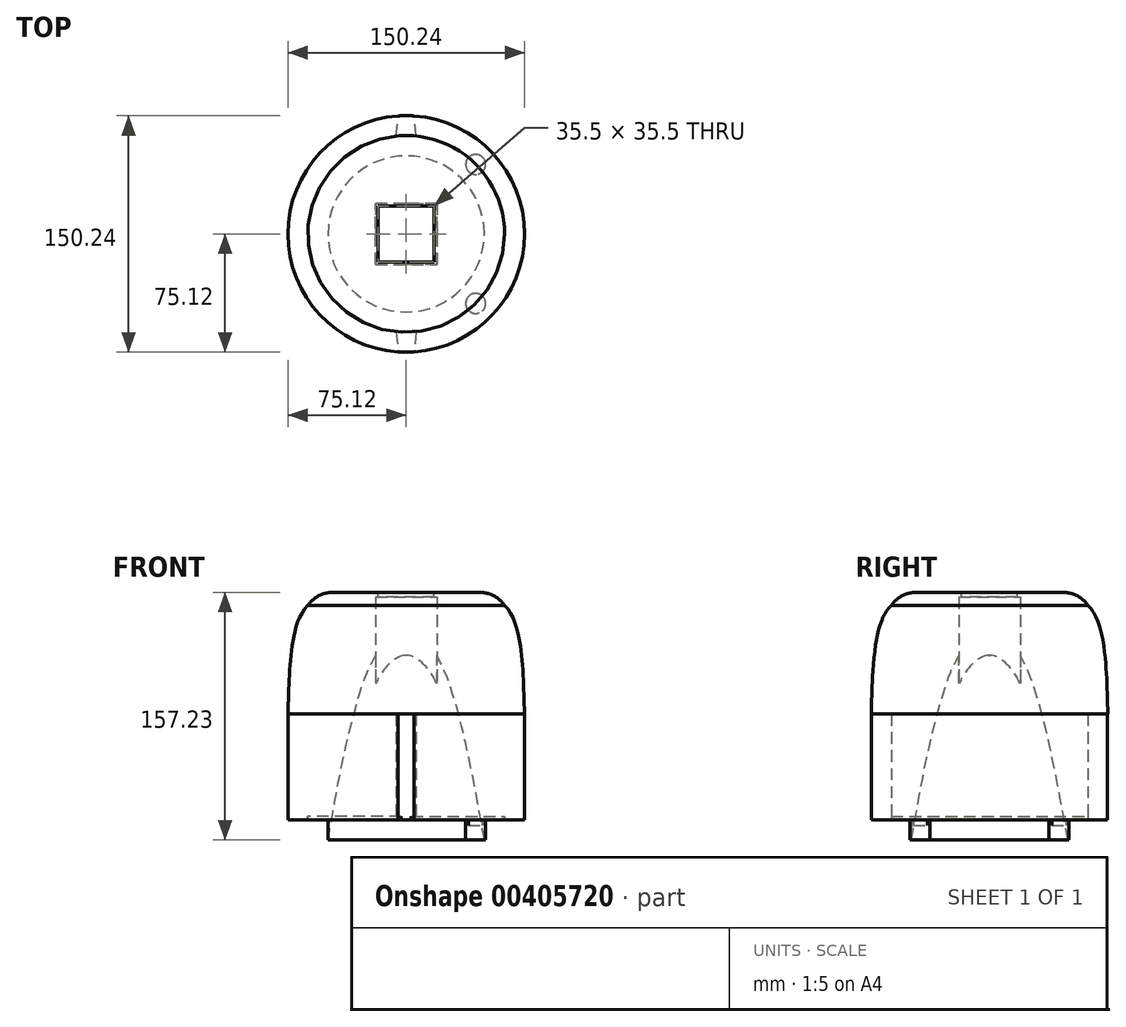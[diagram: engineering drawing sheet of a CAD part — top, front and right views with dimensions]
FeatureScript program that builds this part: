
annotation { "Feature Type Name" : "Feature", "Feature Type Description" : "" }
export const myFeature = defineFeature(function(context is Context, id is Id, definition is map)
    precondition{}
    {
        {
            var Q0;
            Q0=qCreatedBy(makeId("Front.planeOp"),FACE);
            var sketch = newSketch(context, id + "F0", { "sketchPlane" : qUnion([Q0])});
            skLineSegment(sketch, "E0", {"start": v(0, 0) * mm, "end": v(0, 152.4) * mm});
            skLineSegment(sketch, "E1", {"start": v(-50.8, 152.4) * mm, "end": v(-45.72, 152.4) * mm});
            skLineSegment(sketch, "E2", {"start": v(-45.72, 152.4) * mm, "end": v(-45.72, 157.4) * mm});
            skLineSegment(sketch, "E3", {"start": v(-75.12, 0) * mm, "end": v(-62.42, 0) * mm});
            skArc(sketch, "E4", {"start": v(-50.8, 152.4) * mm, "mid": v(-60.05, 76.46) * mm, "end": v(-62.42, 0) * mm});
            skLineSegment(sketch, "E5", {"start": v(-75.12, 0) * mm, "end": v(-75.12, 80) * mm});
            skFitSpline(sketch, "E6", {"points": [v(-75.12, 80) * mm, v(-65.64, 145) * mm, v(-45.72, 157.4) * mm], "startDerivative": vector(3.22, 125.97) * mm, "endDerivative": vector(60.37, 19.92) * mm});
            skSolve(sketch);
        }
        {
            var Q0;
            Q0=makeQuery(id+"F0.imprint","IMPRINT",FACE,{"disambiguationData":[TD([[makeQuery(id+"F0.imprint","IMPRINT",EDGE,{"derivedFrom":sQuery(id+"F0.wireOp",EDGE,"E1")}),1.0]])]});
            var Q1;
            Q1=sQuery(id+"F0.wireOp",EDGE,"E0");
            revolve(context, id + "F1", {"entities" : qUnion([Q0]), "axis" : qUnion([Q1]), "revolveType" : RevolveType.FULL});
        }
        {
            var Q0;
            Q0=qCreatedBy(makeId("Top.planeOp"),FACE);
            var sketch = newSketch(context, id + "F2", { "sketchPlane" : qUnion([Q0])});
            skLineSegment(sketch, "E7.bottom", {"start": v(19.42, 19.42) * mm, "end": v(-19.42, 19.42) * mm});
            skLineSegment(sketch, "E7.top", {"start": v(19.42, -19.42) * mm, "end": v(-19.42, -19.42) * mm});
            skLineSegment(sketch, "E7.left", {"start": v(19.42, 19.42) * mm, "end": v(19.42, -19.42) * mm});
            skLineSegment(sketch, "E7.right", {"start": v(-19.42, 19.42) * mm, "end": v(-19.42, -19.42) * mm});
            skCircle(sketch, "E8", {"center": v(0, 0) * mm, "radius": 62.5 * mm});
            skSolve(sketch);
        }
        {
            var Q0;
            Q0=makeQuery(id+"F2.imprint","IMPRINT",FACE,{"disambiguationData":[TD([[makeQuery(id+"F2.imprint","IMPRINT",EDGE,{"derivedFrom":sQuery(id+"F2.wireOp",EDGE,"E7.bottom")}),-1.0]])]});
            extrude(context, id + "F3", {"entities" : qUnion([Q0]), "operationType" : NewBodyOperationType.ADD, "depth" : 157.39 * mm});
        }
        {
            var Q0;
            Q0=qCreatedBy(makeId("Front.planeOp"),FACE);
            var sketch = newSketch(context, id + "F4", { "sketchPlane" : qUnion([Q0])});
            skLineSegment(sketch, "E9", {"start": v(-68.96, 155.44) * mm, "end": v(-59.58, 163.5) * mm});
            skLineSegment(sketch, "E10", {"start": v(-46.58, 157.23) * mm, "end": v(0, 157.23) * mm});
            skLineSegment(sketch, "E11", {"start": v(0, 157.23) * mm, "end": v(0, 165.56) * mm});
            skLineSegment(sketch, "E12", {"start": v(0, 165.56) * mm, "end": v(-59.58, 163.5) * mm});
            skLineSegment(sketch, "E13", {"start": v(-62.5, 148.83) * mm, "end": v(-68.96, 155.44) * mm});
            skArc(sketch, "E14", {"start": v(-46.58, 157.23) * mm, "mid": v(-55.58, 155) * mm, "end": v(-62.5, 148.83) * mm});
            skSolve(sketch);
        }
        {
            var Q0;
            Q0=qCreatedBy(makeId("Front.planeOp"),FACE);
            var sketch = newSketch(context, id + "F5", { "sketchPlane" : qUnion([Q0])});
            skLineSegment(sketch, "E15", {"start": v(0, 0) * mm, "end": v(-19.43, 0) * mm});
            skLineSegment(sketch, "E16", {"start": v(0, 0) * mm, "end": v(-49.6, 0) * mm});
            skLineSegment(sketch, "E17", {"start": v(-19.43, 117.13) * mm, "end": v(0, 117.13) * mm});
            skLineSegment(sketch, "E18", {"start": v(0, 117.13) * mm, "end": v(0, 0) * mm});
            skFitSpline(sketch, "E19", {"points": [v(-49.6, 0) * mm, v(-38.96, 56.05) * mm, v(-26.46, 102.07) * mm, v(-19.43, 117.13) * mm], "startDerivative": vector(23.85, 136.63) * mm, "endDerivative": vector(31.29, 58.1) * mm});
            skSolve(sketch);
        }
        {
            var Q0;
            Q0 = qSketchRegion(id + "F5", true);
            var Q1;
            Q1=sQuery(id+"F5.wireOp",EDGE,"E18");
            revolve(context, id + "F6", {"operationType" : NewBodyOperationType.REMOVE, "entities" : qUnion([Q0]), "axis" : qUnion([Q1]), "revolveType" : RevolveType.FULL, "oppositeDirection" : true});
        }
        {
            var Q0;
            Q0=makeQuery(id+"F4.imprint","IMPRINT",FACE,{"disambiguationData":[TD([[makeQuery(id+"F4.imprint","IMPRINT",EDGE,{"derivedFrom":sQuery(id+"F4.wireOp",EDGE,"E9")}),-1.0]])]});
            var Q1;
            Q1=sQuery(id+"F4.wireOp",EDGE,"E11");
            revolve(context, id + "F7", {"operationType" : NewBodyOperationType.REMOVE, "entities" : qUnion([Q0]), "axis" : qUnion([Q1]), "revolveType" : RevolveType.FULL, "oppositeDirection" : true});
        }
        {
            var Q0;
            Q0=makeQuery(id+"F7.boolean.opBoolean","COPY",FACE,{"derivedFrom":makeQuery(id+"F7.opRevolve","SWEPT_FACE",FACE,{"disambiguationData":[OSD([sQuery(id+"F4.wireOp",EDGE,"E10")])]})});
            var sketch = newSketch(context, id + "F8", { "sketchPlane" : qUnion([Q0])});
            skLineSegment(sketch, "E20.bottom", {"start": v(17.75, 17.75) * mm, "end": v(-17.75, 17.75) * mm});
            skLineSegment(sketch, "E20.top", {"start": v(17.75, -17.75) * mm, "end": v(-17.75, -17.75) * mm});
            skLineSegment(sketch, "E20.left", {"start": v(17.75, 17.75) * mm, "end": v(17.75, -17.75) * mm});
            skLineSegment(sketch, "E20.right", {"start": v(-17.75, 17.75) * mm, "end": v(-17.75, -17.75) * mm});
            skLineSegment(sketch, "E21.bottom", {"start": v(19.42, 19.42) * mm, "end": v(-19.42, 19.42) * mm});
            skLineSegment(sketch, "E21.top", {"start": v(19.42, -19.42) * mm, "end": v(-19.42, -19.42) * mm});
            skLineSegment(sketch, "E21.left", {"start": v(19.42, 19.42) * mm, "end": v(19.42, -19.42) * mm});
            skLineSegment(sketch, "E21.right", {"start": v(-19.42, 19.42) * mm, "end": v(-19.42, -19.42) * mm});
            skSolve(sketch);
        }
        {
            var Q0;
            Q0=makeQuery(id+"F8.imprint","IMPRINT",FACE,{"disambiguationData":[TD([[makeQuery(id+"F8.imprint","IMPRINT",EDGE,{"derivedFrom":sQuery(id+"F8.wireOp",EDGE,"E20.bottom")}),-1.0]])]});
            extrude(context, id + "F9", {"entities" : qUnion([Q0]), "operationType" : NewBodyOperationType.ADD, "oppositeDirection" : true, "depth" : 3 * mm});
        }
        {
            var Q0;
            Q0=makeQuery(id+"F3.boolean.opBoolean","MERGE",FACE,{"derivedFrom":[makeQuery(id+"F1.opRevolve","SWEPT_FACE",FACE,{"disambiguationData":[OSD([sQuery(id+"F0.wireOp",EDGE,"E3")])]}),makeQuery(id+"F3.opExtrude","CAP_FACE",FACE,{"disambiguationData":[OSD([sQuery(id+"F2.wireOp",EDGE,"E7.bottom"),sQuery(id+"F2.wireOp",EDGE,"E7.top"),sQuery(id+"F2.wireOp",EDGE,"E7.left"),sQuery(id+"F2.wireOp",EDGE,"E7.right"),sQuery(id+"F2.wireOp",EDGE,"E8")])],"isStart":true})]});
            var sketch = newSketch(context, id + "F10", { "sketchPlane" : qUnion([Q0])});
            skLineSegment(sketch, "E22.MirrorCS", {"start": v(6.35, 62.42) * mm, "end": v(5.08, 74.95) * mm});
            skLineSegment(sketch, "E23.MirrorCS", {"start": v(6.35, 62.42) * mm, "end": v(-6.35, 62.42) * mm});
            skLineSegment(sketch, "E24.MirrorCS", {"start": v(-6.35, 62.42) * mm, "end": v(-5.08, 74.95) * mm});
            skLineSegment(sketch, "E25.MirrorCS", {"start": v(6.35, -62.42) * mm, "end": v(-6.35, -62.42) * mm});
            skLineSegment(sketch, "E26.MirrorCS", {"start": v(6.35, -62.42) * mm, "end": v(5.08, -74.95) * mm});
            skLineSegment(sketch, "E27.MirrorCS", {"start": v(-6.35, -62.42) * mm, "end": v(-5.08, -74.95) * mm});
            skArc(sketch, "E28", {"start": v(-5.08, -74.95) * mm, "mid": v(0, -79.54) * mm, "end": v(5.08, -74.95) * mm});
            skArc(sketch, "E29", {"start": v(5.08, 74.95) * mm, "mid": v(0, 79.54) * mm, "end": v(-5.08, 74.95) * mm});
            skSolve(sketch);
        }
        {
            var Q0;
            {var subQ0=sQuery(id+"F10.wireOp",EDGE,"E22.MirrorCS");Q0=makeQuery(id+"F10.imprint","IMPRINT",FACE,{"disambiguationData":[TD([[makeQuery(id+"F10.imprint","IMPRINT",EDGE,{"derivedFrom":subQ0}),1.0]])]});}
            var Q1;
            {var subQ0=sQuery(id+"F10.wireOp",EDGE,"E29");Q1=makeQuery(id+"F10.imprint","IMPRINT",FACE,{"disambiguationData":[TD([[makeQuery(id+"F10.imprint","IMPRINT",EDGE,{"derivedFrom":subQ0}),1.0]])]});}
            var Q2;
            {var subQ0=sQuery(id+"F10.wireOp",EDGE,"pWpjYdiS-psPs-4qNo-ci7S-aIeb0pvxVKC6");Q2=makeQuery(id+"F10.imprint","IMPRINT",FACE,{"disambiguationData":[TD([[makeQuery(id+"F10.imprint","IMPRINT",EDGE,{"derivedFrom":subQ0}),1.0]])]});}
            var Q3;
            {var subQ0=sQuery(id+"F10.wireOp",EDGE,"qUAnafuY-LLeP-OAQ9-itBr-fdHKaFW8QgKj");Q3=makeQuery(id+"F10.imprint","IMPRINT",FACE,{"disambiguationData":[TD([[makeQuery(id+"F10.imprint","IMPRINT",EDGE,{"derivedFrom":subQ0}),1.0]])]});}
            var Q4;
            {var subQ0=sQuery(id+"F10.wireOp",EDGE,"e09f1899-c965-4668-bec3-c89c10b5707f0.MirrorCS");Q4=makeQuery(id+"F10.imprint","IMPRINT",FACE,{"disambiguationData":[TD([[makeQuery(id+"F10.imprint","IMPRINT",EDGE,{"derivedFrom":subQ0}),-1.0]])]});}
            var Q5;
            {var subQ0=sQuery(id+"F10.wireOp",EDGE,"gZlWP4jL-bsxm-O0XO-Gu2L-qvSfP1H2f6X3");Q5=makeQuery(id+"F10.imprint","IMPRINT",FACE,{"disambiguationData":[TD([[makeQuery(id+"F10.imprint","IMPRINT",EDGE,{"derivedFrom":subQ0}),1.0]])]});}
            var Q6;
            Q6=makeQuery(id+"F10.imprint","IMPRINT",FACE,{"disambiguationData":[TD([[makeQuery(id+"F10.imprint","IMPRINT",EDGE,{"derivedFrom":sQuery(id+"F10.wireOp",EDGE,"E25.MirrorCS")}),1.0]])]});
            var Q7;
            {var subQ0=sQuery(id+"F10.wireOp",EDGE,"E28");Q7=makeQuery(id+"F10.imprint","IMPRINT",FACE,{"disambiguationData":[TD([[makeQuery(id+"F10.imprint","IMPRINT",EDGE,{"derivedFrom":subQ0}),1.0]])]});}
            extrude(context, id + "F11", {"entities" : qUnion([Q0, Q1, Q2, Q3, Q4, Q5, Q6, Q7]), "operationType" : NewBodyOperationType.REMOVE, "oppositeDirection" : true, "depth" : 80 * mm});
        }
        {
            var Q0;
            Q0=makeQuery(id+"F3.boolean.opBoolean","MERGE",FACE,{"derivedFrom":[makeQuery(id+"F1.opRevolve","SWEPT_FACE",FACE,{"disambiguationData":[OSD([sQuery(id+"F0.wireOp",EDGE,"E3")])]}),makeQuery(id+"F3.opExtrude","CAP_FACE",FACE,{"disambiguationData":[OSD([sQuery(id+"F2.wireOp",EDGE,"E7.bottom"),sQuery(id+"F2.wireOp",EDGE,"E7.top"),sQuery(id+"F2.wireOp",EDGE,"E7.left"),sQuery(id+"F2.wireOp",EDGE,"E7.right"),sQuery(id+"F2.wireOp",EDGE,"E8")])],"isStart":true})]});
            var sketch = newSketch(context, id + "F12", { "sketchPlane" : qUnion([Q0])});
            skCircle(sketch, "E30", {"center": v(-44.14, 44.14) * mm, "radius": 6.35 * mm});
            skCircle(sketch, "E31.MirrorC", {"center": v(44.14, -44.14) * mm, "radius": 6.35 * mm});
            skCircle(sketch, "E32.MirrorC", {"center": v(-44.14, -44.14) * mm, "radius": 6.35 * mm});
            skCircle(sketch, "E33.MirrorC", {"center": v(44.14, 44.14) * mm, "radius": 6.35 * mm});
            skSolve(sketch);
        }
        {
            var Q0;
            Q0=makeQuery(id+"F12.imprint","IMPRINT",FACE,{"disambiguationData":[TD([[makeQuery(id+"F12.imprint","IMPRINT",EDGE,{"derivedFrom":sQuery(id+"F12.wireOp",EDGE,"E30")}),1.0]])]});
            var Q1;
            Q1=makeQuery(id+"F12.imprint","IMPRINT",FACE,{"disambiguationData":[TD([[makeQuery(id+"F12.imprint","IMPRINT",EDGE,{"derivedFrom":sQuery(id+"F12.wireOp",EDGE,"E33.MirrorC")}),-1.0]])]});
            var Q2;
            Q2=makeQuery(id+"F12.imprint","IMPRINT",FACE,{"disambiguationData":[TD([[makeQuery(id+"F12.imprint","IMPRINT",EDGE,{"derivedFrom":sQuery(id+"F12.wireOp",EDGE,"E31.MirrorC")}),-1.0]])]});
            var Q3;
            Q3=makeQuery(id+"F12.imprint","IMPRINT",FACE,{"disambiguationData":[TD([[makeQuery(id+"F12.imprint","IMPRINT",EDGE,{"derivedFrom":sQuery(id+"F12.wireOp",EDGE,"E32.MirrorC")}),1.0]])]});
            extrude(context, id + "F13", {"entities" : qUnion([Q0, Q1, Q2, Q3]), "operationType" : NewBodyOperationType.REMOVE, "oppositeDirection" : true, "depth" : 12.7 * mm});
        }
    });
